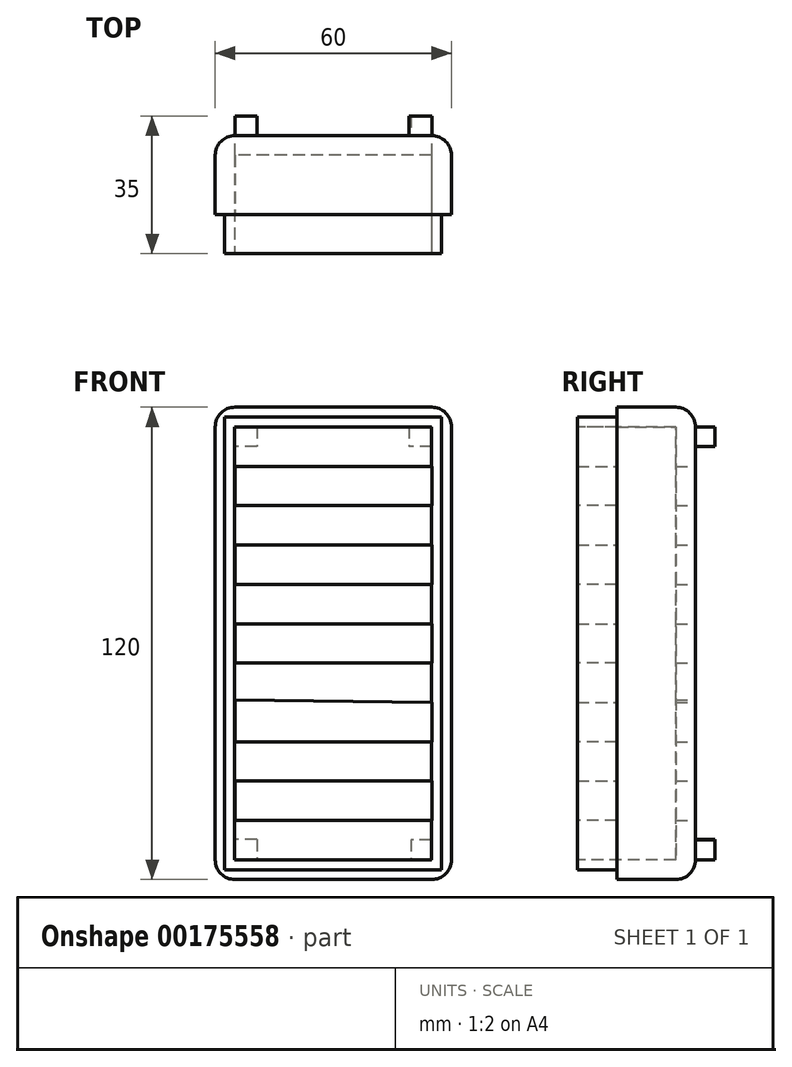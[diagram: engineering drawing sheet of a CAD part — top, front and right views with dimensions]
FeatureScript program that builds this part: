
annotation { "Feature Type Name" : "Feature", "Feature Type Description" : "" }
export const myFeature = defineFeature(function(context is Context, id is Id, definition is map)
    precondition{}
    {
        {
            var Q0;
            Q0=qCreatedBy(makeId("Front.planeOp"),FACE);
            var sketch = newSketch(context, id + "F0", { "sketchPlane" : qUnion([Q0])});
            skLineSegment(sketch, "E0.bottom", {"start": v(-33.73, 74.3) * mm, "end": v(26.27, 74.3) * mm});
            skLineSegment(sketch, "E0.top", {"start": v(-33.73, -45.7) * mm, "end": v(26.27, -45.7) * mm});
            skLineSegment(sketch, "E0.left", {"start": v(-33.73, 74.3) * mm, "end": v(-33.73, -45.7) * mm});
            skLineSegment(sketch, "E0.right", {"start": v(26.27, 74.3) * mm, "end": v(26.27, -45.7) * mm});
            skPoint(sketch, "E1.top.end.orphan", {"position": v(0, 16.6) * mm});
            skLineSegment(sketch, "E2.bottom", {"start": v(-28.73, 69.3) * mm, "end": v(21.27, 69.3) * mm});
            skLineSegment(sketch, "E2.top", {"start": v(-28.73, -40.7) * mm, "end": v(21.27, -40.7) * mm});
            skLineSegment(sketch, "E2.left", {"start": v(-28.73, 69.3) * mm, "end": v(-28.73, -40.7) * mm});
            skLineSegment(sketch, "E2.right", {"start": v(21.27, 69.3) * mm, "end": v(21.27, -40.7) * mm});
            skLineSegment(sketch, "E3", {"start": v(-33.73, 74.3) * mm, "end": v(-31.23, 74.3) * mm});
            skLineSegment(sketch, "E4.bottom", {"start": v(-31.23, 71.8) * mm, "end": v(23.77, 71.8) * mm});
            skLineSegment(sketch, "E4.top", {"start": v(-31.23, -43.2) * mm, "end": v(23.77, -43.2) * mm});
            skLineSegment(sketch, "E4.left", {"start": v(-31.23, 71.8) * mm, "end": v(-31.23, -43.2) * mm});
            skLineSegment(sketch, "E4.right", {"start": v(23.77, 71.8) * mm, "end": v(23.77, -43.2) * mm});
            skPoint(sketch, "E5.start.orphan", {"position": v(-31.23, 74.3) * mm});
            skPoint(sketch, "E6.orphan", {"position": v(-28.73, 74.3) * mm});
            skSolve(sketch);
        }
        {
            var Q0;
            Q0=makeQuery(id+"F0.imprint","IMPRINT",FACE,{"disambiguationData":[TD([[makeQuery(id+"F0.imprint","IMPRINT",EDGE,{"derivedFrom":sQuery(id+"F0.wireOp",EDGE,"E0.bottom")}),-1.0]])]});
            var Q1;
            Q1=makeQuery(id+"F0.imprint","IMPRINT",FACE,{"disambiguationData":[TD([[makeQuery(id+"F0.imprint","IMPRINT",EDGE,{"derivedFrom":sQuery(id+"F0.wireOp",EDGE,"E2.bottom")}),1.0]])]});
            extrude(context, id + "F1", {"entities" : qUnion([Q0, Q1]), "depth" : 20 * mm});
        }
        {
            var Q0;
            Q0=qCreatedBy(makeId("Front.planeOp"),FACE);
            cPlane(context, id + "F2", {"entities" : qUnion([Q0]), "cplaneType" : CPlaneType.OFFSET, "offset" : 20 * mm, "width" : 150 * mm, "height" : 150 * mm});
        }
        {
            var Q0;
            Q0=qCreatedBy(id+"F2.planeOp",FACE);
            var sketch = newSketch(context, id + "F3", { "sketchPlane" : qUnion([Q0])});
            skLineSegment(sketch, "E7", {"start": v(26.19, 74.28) * mm, "end": v(26.19, 71.78) * mm});
            skLineSegment(sketch, "E8", {"start": v(26.19, 71.78) * mm, "end": v(23.69, 71.78) * mm});
            skLineSegment(sketch, "E9", {"start": v(23.69, 71.78) * mm, "end": v(23.69, -43.22) * mm});
            skLineSegment(sketch, "E10", {"start": v(23.69, -43.22) * mm, "end": v(-31.31, -43.22) * mm});
            skLineSegment(sketch, "E11", {"start": v(-31.31, -43.22) * mm, "end": v(-31.31, 71.78) * mm});
            skLineSegment(sketch, "E12", {"start": v(-31.31, 71.78) * mm, "end": v(23.69, 71.78) * mm});
            skSolve(sketch);
        }
        {
            var Q0;
            Q0=qCreatedBy(id+"F2.planeOp",FACE);
            var sketch = newSketch(context, id + "F4", { "sketchPlane" : qUnion([Q0])});
            skLineSegment(sketch, "E13", {"start": v(21.32, -40.9) * mm, "end": v(-28.68, -40.9) * mm});
            skLineSegment(sketch, "E14", {"start": v(-28.68, -40.9) * mm, "end": v(-28.68, 69.06) * mm});
            skLineSegment(sketch, "E15", {"start": v(-28.68, 69.06) * mm, "end": v(20.24, 69.06) * mm});
            skLineSegment(sketch, "E16", {"start": v(20.24, 69.06) * mm, "end": v(21.32, -40.9) * mm});
            skSolve(sketch);
        }
        {
            var Q0;
            Q0=makeQuery(id+"F3.imprint","IMPRINT",FACE,{"disambiguationData":[TD([[makeQuery(id+"F3.imprint","IMPRINT",EDGE,{"derivedFrom":sQuery(id+"F3.wireOp",EDGE,"E9")}),-1.0]])]});
            var Q1;
            Q1=makeQuery(id+"F4.imprint","IMPRINT",FACE,{"disambiguationData":[TD([[makeQuery(id+"F4.imprint","IMPRINT",EDGE,{"derivedFrom":sQuery(id+"F4.wireOp",EDGE,"E13")}),-1.0]])]});
            extrude(context, id + "F5", {"entities" : qUnion([Q0, Q1]), "operationType" : NewBodyOperationType.ADD, "depth" : 10 * mm});
        }
        {
            var Q0;
            Q0=makeQuery(id+"F5.opExtrude","CAP_FACE",FACE,{"disambiguationData":[OSD([sQuery(id+"F3.wireOp",EDGE,"E9"),sQuery(id+"F3.wireOp",EDGE,"E10"),sQuery(id+"F3.wireOp",EDGE,"E11"),sQuery(id+"F3.wireOp",EDGE,"E12")])],"isStart":false});
            var sketch = newSketch(context, id + "F6", { "sketchPlane" : qUnion([Q0])});
            skLineSegment(sketch, "E17", {"start": v(23.69, 71.78) * mm, "end": v(23.69, 69.28) * mm});
            skLineSegment(sketch, "E18", {"start": v(23.69, 69.28) * mm, "end": v(21.19, 69.28) * mm});
            skLineSegment(sketch, "E19.bottom", {"start": v(21.19, 69.28) * mm, "end": v(-28.81, 69.28) * mm});
            skLineSegment(sketch, "E19.top", {"start": v(21.19, -40.72) * mm, "end": v(-28.81, -40.72) * mm});
            skLineSegment(sketch, "E19.left", {"start": v(21.19, 69.28) * mm, "end": v(21.19, -40.72) * mm});
            skLineSegment(sketch, "E19.right", {"start": v(-28.81, 69.28) * mm, "end": v(-28.81, -40.72) * mm});
            skSolve(sketch);
        }
        {
            var Q0;
            Q0=makeQuery(id+"F6.imprint","IMPRINT",FACE,{"disambiguationData":[TD([[makeQuery(id+"F6.imprint","IMPRINT",EDGE,{"derivedFrom":sQuery(id+"F6.wireOp",EDGE,"E19.bottom")}),1.0]])]});
            extrude(context, id + "F7", {"entities" : qUnion([Q0]), "operationType" : NewBodyOperationType.REMOVE, "oppositeDirection" : true, "depth" : 215.8 * mm});
        }
        {
            var Q0;
            Q0=makeQuery(id+"F1.opExtrude","CAP_FACE",FACE,{"disambiguationData":[OSD([sQuery(id+"F0.wireOp",EDGE,"E0.bottom"),sQuery(id+"F0.wireOp",EDGE,"E0.top"),sQuery(id+"F0.wireOp",EDGE,"E0.left"),sQuery(id+"F0.wireOp",EDGE,"E0.right"),sQuery(id+"F0.wireOp",EDGE,"E2.bottom"),sQuery(id+"F0.wireOp",EDGE,"E2.top"),sQuery(id+"F0.wireOp",EDGE,"E2.left"),sQuery(id+"F0.wireOp",EDGE,"E2.right"),sQuery(id+"F0.wireOp",EDGE,"E3")])],"isStart":true});
            var sketch = newSketch(context, id + "F8", { "sketchPlane" : qUnion([Q0])});
            skLineSegment(sketch, "E20.bottom", {"start": v(-26.27, 74.3) * mm, "end": v(33.73, 74.3) * mm});
            skLineSegment(sketch, "E20.top", {"start": v(-26.27, -45.7) * mm, "end": v(33.73, -45.7) * mm});
            skLineSegment(sketch, "E20.left", {"start": v(-26.27, 74.3) * mm, "end": v(-26.27, -45.7) * mm});
            skLineSegment(sketch, "E20.right", {"start": v(33.73, 74.3) * mm, "end": v(33.73, -45.7) * mm});
            skSolve(sketch);
        }
        {
            var Q0;
            Q0 = qSketchRegion(id + "F8", true);
            extrude(context, id + "F9", {"entities" : qUnion([Q0]), "operationType" : NewBodyOperationType.ADD, "oppositeDirection" : true, "depth" : 5 * mm});
        }
        {
            var Q0;
            Q0=makeQuery(id+"F9.boolean.opBoolean","MERGE",FACE,{"derivedFrom":[makeQuery(id+"F1.opExtrude","CAP_FACE",FACE,{"disambiguationData":[OSD([sQuery(id+"F0.wireOp",EDGE,"E0.bottom"),sQuery(id+"F0.wireOp",EDGE,"E0.top"),sQuery(id+"F0.wireOp",EDGE,"E0.left"),sQuery(id+"F0.wireOp",EDGE,"E0.right"),sQuery(id+"F0.wireOp",EDGE,"E2.bottom"),sQuery(id+"F0.wireOp",EDGE,"E2.top"),sQuery(id+"F0.wireOp",EDGE,"E2.left"),sQuery(id+"F0.wireOp",EDGE,"E2.right"),sQuery(id+"F0.wireOp",EDGE,"E3")])],"isStart":true}),makeQuery(id+"F9.opExtrude","CAP_FACE",FACE,{"disambiguationData":[OSD([sQuery(id+"F8.wireOp",EDGE,"E20.bottom"),sQuery(id+"F8.wireOp",EDGE,"E20.top"),sQuery(id+"F8.wireOp",EDGE,"E20.left"),sQuery(id+"F8.wireOp",EDGE,"E20.right")])],"isStart":true})]});
            var sketch = newSketch(context, id + "F10", { "sketchPlane" : qUnion([Q0])});
            skLineSegment(sketch, "E21", {"start": v(-26.27, -45.7) * mm, "end": v(-21.27, -45.7) * mm});
            skLineSegment(sketch, "E22", {"start": v(-21.27, -45.7) * mm, "end": v(-21.27, -30.7) * mm});
            skLineSegment(sketch, "E23", {"start": v(-21.27, -30.7) * mm, "end": v(-21.27, -20.7) * mm});
            skLineSegment(sketch, "E24", {"start": v(-21.27, -20.7) * mm, "end": v(-21.27, -10.7) * mm});
            skPoint(sketch, "E24.endSnap0", {"position": v(-21.27, -25.7) * mm});
            skLineSegment(sketch, "E25", {"start": v(-21.27, -10.7) * mm, "end": v(-21.27, -0.7) * mm});
            skPoint(sketch, "E26.endSnap0", {"position": v(-26.27, 14.3) * mm});
            skPoint(sketch, "E26.endSnap1", {"position": v(-21.27, -5.7) * mm});
            skPoint(sketch, "E26.end.orphan", {"position": v(-21.27, 14.3) * mm});
            skLineSegment(sketch, "E27", {"start": v(-21.27, -0.7) * mm, "end": v(-21.27, 9.3) * mm});
            skLineSegment(sketch, "E28", {"start": v(-21.27, 9.3) * mm, "end": v(-21.27, 19.3) * mm});
            skLineSegment(sketch, "E29", {"start": v(-21.27, 19.3) * mm, "end": v(-21.27, 29.3) * mm});
            skLineSegment(sketch, "E30", {"start": v(-21.27, 29.3) * mm, "end": v(-21.27, 39.3) * mm});
            skLineSegment(sketch, "E31", {"start": v(-21.27, 39.3) * mm, "end": v(-21.27, 49.3) * mm});
            skLineSegment(sketch, "E32", {"start": v(-21.27, 49.3) * mm, "end": v(-21.27, 59.3) * mm});
            skLineSegment(sketch, "E33", {"start": v(-21.27, 59.3) * mm, "end": v(-21.27, 74.3) * mm});
            skLineSegment(sketch, "E34", {"start": v(-21.27, -30.7) * mm, "end": v(28.73, -30.7) * mm});
            skLineSegment(sketch, "E35", {"start": v(28.73, -30.7) * mm, "end": v(28.73, -20.7) * mm});
            skLineSegment(sketch, "E36", {"start": v(28.73, -20.7) * mm, "end": v(-21.27, -20.7) * mm});
            skLineSegment(sketch, "E37", {"start": v(-21.27, -10.7) * mm, "end": v(28.73, -10.7) * mm});
            skLineSegment(sketch, "E38", {"start": v(28.73, -10.7) * mm, "end": v(28.73, 0) * mm});
            skLineSegment(sketch, "E39", {"start": v(28.73, 0) * mm, "end": v(-21.27, -0.7) * mm});
            skLineSegment(sketch, "E40", {"start": v(-21.27, 9.3) * mm, "end": v(28.73, 9.3) * mm});
            skLineSegment(sketch, "E41", {"start": v(28.73, 9.3) * mm, "end": v(28.73, 19.3) * mm});
            skLineSegment(sketch, "E42", {"start": v(28.73, 19.3) * mm, "end": v(-21.27, 19.3) * mm});
            skLineSegment(sketch, "E43", {"start": v(-21.27, 29.3) * mm, "end": v(28.73, 29.3) * mm});
            skLineSegment(sketch, "E44", {"start": v(28.73, 29.3) * mm, "end": v(28.73, 39.3) * mm});
            skLineSegment(sketch, "E45", {"start": v(28.73, 39.3) * mm, "end": v(-21.27, 39.3) * mm});
            skLineSegment(sketch, "E46", {"start": v(-21.27, 49.3) * mm, "end": v(28.73, 49.3) * mm});
            skLineSegment(sketch, "E47", {"start": v(28.73, 49.3) * mm, "end": v(28.73, 59.3) * mm});
            skLineSegment(sketch, "E48", {"start": v(28.73, 59.3) * mm, "end": v(-21.27, 59.3) * mm});
            skSolve(sketch);
        }
        {
            var Q0;
            Q0=qCreatedBy(makeId("Front.planeOp"),FACE);
            var sketch = newSketch(context, id + "F11", { "sketchPlane" : qUnion([Q0])});
            skSolve(sketch);
        }
        {
            var Q0;
            Q0 = qSketchRegion(id + "F11", true);
            var Q1;
            Q1=makeQuery(id+"F10.imprint","IMPRINT",FACE,{"disambiguationData":[TD([[makeQuery(id+"F10.imprint","IMPRINT",EDGE,{"derivedFrom":sQuery(id+"F10.wireOp",EDGE,"E32")}),-1.0]])]});
            var Q2;
            Q2=makeQuery(id+"F10.imprint","IMPRINT",FACE,{"disambiguationData":[TD([[makeQuery(id+"F10.imprint","IMPRINT",EDGE,{"derivedFrom":sQuery(id+"F10.wireOp",EDGE,"E30")}),-1.0]])]});
            var Q3;
            Q3=makeQuery(id+"F10.imprint","IMPRINT",FACE,{"disambiguationData":[TD([[makeQuery(id+"F10.imprint","IMPRINT",EDGE,{"derivedFrom":sQuery(id+"F10.wireOp",EDGE,"E28")}),-1.0]])]});
            var Q4;
            Q4=makeQuery(id+"F10.imprint","IMPRINT",FACE,{"disambiguationData":[TD([[makeQuery(id+"F10.imprint","IMPRINT",EDGE,{"derivedFrom":sQuery(id+"F10.wireOp",EDGE,"E25")}),-1.0]])]});
            var Q5;
            Q5=makeQuery(id+"F10.imprint","IMPRINT",FACE,{"disambiguationData":[TD([[makeQuery(id+"F10.imprint","IMPRINT",EDGE,{"derivedFrom":sQuery(id+"F10.wireOp",EDGE,"E23")}),-1.0]])]});
            extrude(context, id + "F12", {"entities" : qUnion([Q0, Q1, Q2, Q3, Q4, Q5]), "operationType" : NewBodyOperationType.REMOVE, "endBound" : BoundingType.THROUGH_ALL, "oppositeDirection" : true, "depth" : 25 * mm});
        }
        {
            var Q0;
            Q0=makeQuery(id+"F1.opExtrude","CAP_EDGE",EDGE,{"disambiguationData":[OSD([sQuery(id+"F0.wireOp",EDGE,"E0.top")])],"isStart":true});
            var Q1;
            Q1=makeQuery(id+"F1.opExtrude","CAP_EDGE",EDGE,{"disambiguationData":[OSD([sQuery(id+"F0.wireOp",EDGE,"E0.left")])],"isStart":true});
            var Q2;
            Q2=makeQuery(id+"F1.opExtrude","CAP_EDGE",EDGE,{"disambiguationData":[OSD([sQuery(id+"F0.wireOp",EDGE,"E0.right")])],"isStart":true});
            var Q3;
            Q3=makeQuery(id+"F1.opExtrude","CAP_EDGE",EDGE,{"disambiguationData":[OSD([sQuery(id+"F0.wireOp",EDGE,"E0.bottom"),sQuery(id+"F0.wireOp",EDGE,"E3")])],"isStart":true});
            var Q4;
            Q4=makeQuery(id+"F1.opExtrude","SWEPT_EDGE",EDGE,{"disambiguationData":[OSD([sQuery(id+"F0.wireOp",EDGE,"E0.top"),sQuery(id+"F0.wireOp",EDGE,"E0.right")])]});
            var Q5;
            Q5=makeQuery(id+"F1.opExtrude","SWEPT_EDGE",EDGE,{"disambiguationData":[OSD([sQuery(id+"F0.wireOp",EDGE,"E0.bottom"),sQuery(id+"F0.wireOp",EDGE,"E0.right")])]});
            var Q6;
            Q6=makeQuery(id+"F1.opExtrude","SWEPT_EDGE",EDGE,{"disambiguationData":[OSD([sQuery(id+"F0.wireOp",EDGE,"E0.top"),sQuery(id+"F0.wireOp",EDGE,"E0.left")])]});
            var Q7;
            Q7=makeQuery(id+"F1.opExtrude","SWEPT_EDGE",EDGE,{"disambiguationData":[OSD([sQuery(id+"F0.wireOp",EDGE,"E0.left"),sQuery(id+"F0.wireOp",EDGE,"E3")])]});
            fillet(context, id + "F13", {"entities" : qUnion([Q0, Q1, Q2, Q3, Q4, Q5, Q6, Q7]), "radius" : 5 * mm, "tangentPropagation" : true, "allowEdgeOverflow" : false});
        }
        {
            var Q0;
            Q0=makeQuery(id+"F13.opFillet","SPLIT",FACE,{"disambiguationData":[OD(5.0)],"derivedFrom":makeQuery(id+"F9.boolean.opBoolean","MERGE",FACE,{"derivedFrom":[makeQuery(id+"F1.opExtrude","CAP_FACE",FACE,{"disambiguationData":[OSD([sQuery(id+"F0.wireOp",EDGE,"E0.bottom"),sQuery(id+"F0.wireOp",EDGE,"E0.top"),sQuery(id+"F0.wireOp",EDGE,"E0.left"),sQuery(id+"F0.wireOp",EDGE,"E0.right"),sQuery(id+"F0.wireOp",EDGE,"E2.bottom"),sQuery(id+"F0.wireOp",EDGE,"E2.top"),sQuery(id+"F0.wireOp",EDGE,"E2.left"),sQuery(id+"F0.wireOp",EDGE,"E2.right"),sQuery(id+"F0.wireOp",EDGE,"E3")])],"isStart":true}),makeQuery(id+"F9.opExtrude","CAP_FACE",FACE,{"disambiguationData":[OSD([sQuery(id+"F8.wireOp",EDGE,"E20.bottom"),sQuery(id+"F8.wireOp",EDGE,"E20.top"),sQuery(id+"F8.wireOp",EDGE,"E20.left"),sQuery(id+"F8.wireOp",EDGE,"E20.right")])],"isStart":true})]})});
            var sketch = newSketch(context, id + "F14", { "sketchPlane" : qUnion([Q0])});
            skPoint(sketch, "E49.oppositeSnap0", {"position": v(-21.27, 64.3) * mm});
            skLineSegment(sketch, "E49.bottom", {"start": v(-21.27, 69.3) * mm, "end": v(-15.54, 69.3) * mm});
            skLineSegment(sketch, "E49.top", {"start": v(-21.27, 64.3) * mm, "end": v(-15.54, 64.3) * mm});
            skLineSegment(sketch, "E49.left", {"start": v(-21.27, 69.3) * mm, "end": v(-21.27, 64.3) * mm});
            skLineSegment(sketch, "E49.right", {"start": v(-15.54, 69.3) * mm, "end": v(-15.54, 64.3) * mm});
            skLineSegment(sketch, "E50.bottom", {"start": v(-21.22, -35.57) * mm, "end": v(-15.97, -35.57) * mm});
            skLineSegment(sketch, "E50.top", {"start": v(-21.22, -40.64) * mm, "end": v(-15.97, -40.64) * mm});
            skLineSegment(sketch, "E50.left", {"start": v(-21.22, -35.57) * mm, "end": v(-21.22, -40.64) * mm});
            skLineSegment(sketch, "E50.right", {"start": v(-15.97, -35.57) * mm, "end": v(-15.97, -40.64) * mm});
            skSolve(sketch);
        }
        {
            var Q0;
            Q0 = qSketchRegion(id + "F14", true);
            extrude(context, id + "F15", {"entities" : qUnion([Q0]), "operationType" : NewBodyOperationType.ADD, "depth" : 5 * mm});
        }
        {
            var Q0;
            Q0=makeQuery(id+"F13.opFillet","SPLIT",FACE,{"disambiguationData":[OD(5.0)],"derivedFrom":makeQuery(id+"F9.boolean.opBoolean","MERGE",FACE,{"derivedFrom":[makeQuery(id+"F1.opExtrude","CAP_FACE",FACE,{"disambiguationData":[OSD([sQuery(id+"F0.wireOp",EDGE,"E0.bottom"),sQuery(id+"F0.wireOp",EDGE,"E0.top"),sQuery(id+"F0.wireOp",EDGE,"E0.left"),sQuery(id+"F0.wireOp",EDGE,"E0.right"),sQuery(id+"F0.wireOp",EDGE,"E2.bottom"),sQuery(id+"F0.wireOp",EDGE,"E2.top"),sQuery(id+"F0.wireOp",EDGE,"E2.left"),sQuery(id+"F0.wireOp",EDGE,"E2.right"),sQuery(id+"F0.wireOp",EDGE,"E3")])],"isStart":true}),makeQuery(id+"F9.opExtrude","CAP_FACE",FACE,{"disambiguationData":[OSD([sQuery(id+"F8.wireOp",EDGE,"E20.bottom"),sQuery(id+"F8.wireOp",EDGE,"E20.top"),sQuery(id+"F8.wireOp",EDGE,"E20.left"),sQuery(id+"F8.wireOp",EDGE,"E20.right")])],"isStart":true})]})});
            var sketch = newSketch(context, id + "F16", { "sketchPlane" : qUnion([Q0])});
            skLineSegment(sketch, "E51.bottom", {"start": v(23.15, 69.3) * mm, "end": v(28.73, 69.3) * mm});
            skLineSegment(sketch, "E51.top", {"start": v(23.15, 64.3) * mm, "end": v(28.73, 64.3) * mm});
            skLineSegment(sketch, "E51.left", {"start": v(23.15, 69.3) * mm, "end": v(23.15, 64.3) * mm});
            skLineSegment(sketch, "E51.right", {"start": v(28.73, 69.3) * mm, "end": v(28.73, 64.3) * mm});
            skLineSegment(sketch, "E52.bottom", {"start": v(23.15, -35.5) * mm, "end": v(28.73, -35.5) * mm});
            skLineSegment(sketch, "E52.top", {"start": v(23.15, -40.67) * mm, "end": v(28.73, -40.67) * mm});
            skLineSegment(sketch, "E52.left", {"start": v(23.15, -35.5) * mm, "end": v(23.15, -40.67) * mm});
            skLineSegment(sketch, "E52.right", {"start": v(28.73, -35.5) * mm, "end": v(28.73, -40.67) * mm});
            skSolve(sketch);
        }
        {
            var Q0;
            Q0 = qSketchRegion(id + "F16", true);
            extrude(context, id + "F17", {"entities" : qUnion([Q0]), "operationType" : NewBodyOperationType.ADD, "depth" : 5 * mm});
        }
    });
